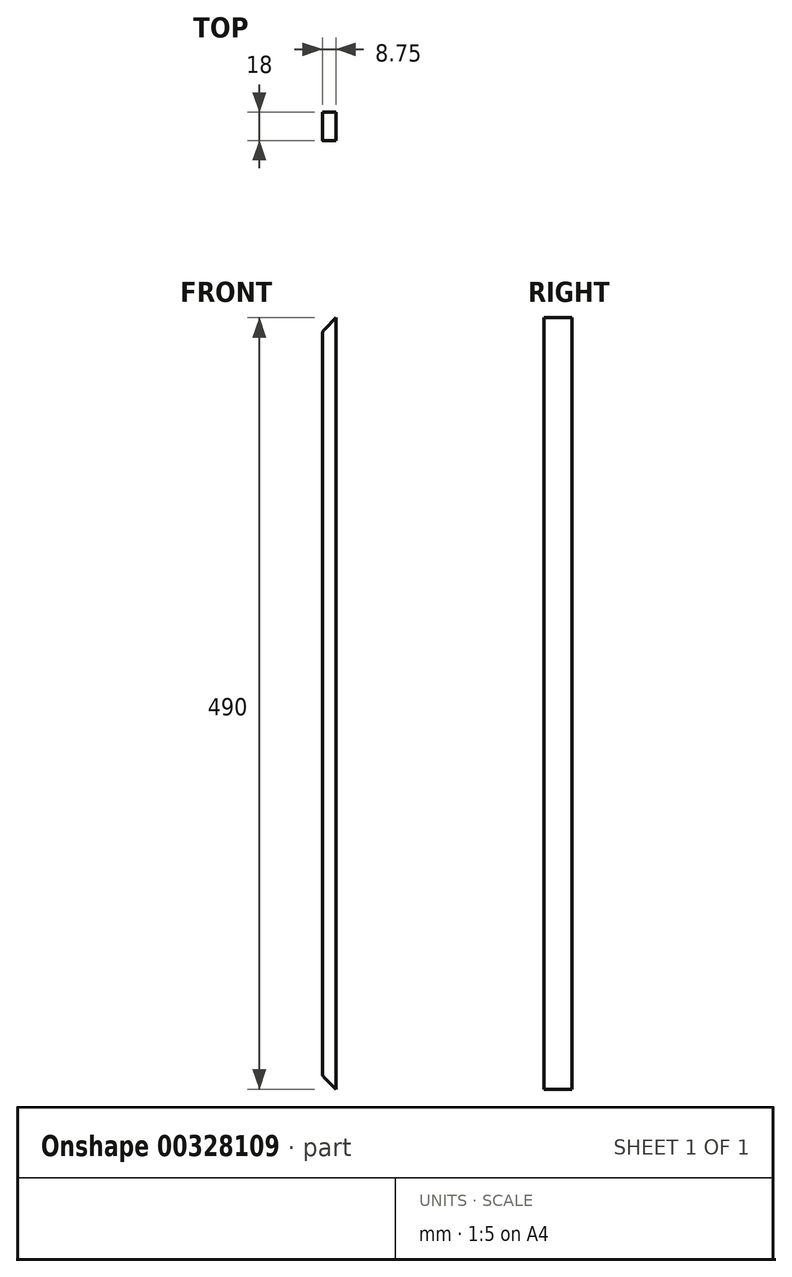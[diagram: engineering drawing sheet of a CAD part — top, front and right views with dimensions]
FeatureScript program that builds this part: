
annotation { "Feature Type Name" : "Feature", "Feature Type Description" : "" }
export const myFeature = defineFeature(function(context is Context, id is Id, definition is map)
    precondition{}
    {
        {
            var Q0;
            Q0=qCreatedBy(makeId("Front.planeOp"),FACE);
            var sketch = newSketch(context, id + "F0", { "sketchPlane" : qUnion([Q0])});
            skLineSegment(sketch, "E0", {"start": v(-9.08, -149.17) * mm, "end": v(-1.65, -156.6) * mm});
            skLineSegment(sketch, "E1", {"start": v(-1.65, -156.6) * mm, "end": v(-1.5, 333.4) * mm});
            skLineSegment(sketch, "E2", {"start": v(-1.5, 333.4) * mm, "end": v(-8.94, 325.96) * mm});
            skArc(sketch, "E3", {"start": v(-8.94, 325.96) * mm, "mid": v(-9.8, 324.67) * mm, "end": v(-10.11, 323.13) * mm});
            skLineSegment(sketch, "E4", {"start": v(-10.11, 323.13) * mm, "end": v(-10.25, -146.34) * mm});
            skArc(sketch, "E5", {"start": v(-10.25, -146.34) * mm, "mid": v(-9.94, -147.87) * mm, "end": v(-9.08, -149.17) * mm});
            skSolve(sketch);
        }
        {
            var Q0;
            Q0=makeQuery(id+"F0.imprint","IMPRINT",FACE,{"disambiguationData":[TD([[makeQuery(id+"F0.imprint","IMPRINT",EDGE,{"derivedFrom":sQuery(id+"F0.wireOp",EDGE,"E0")}),1.0]])]});
            extrude(context, id + "F1", {"entities" : qUnion([Q0]), "depth" : 18 * mm});
        }
    });
